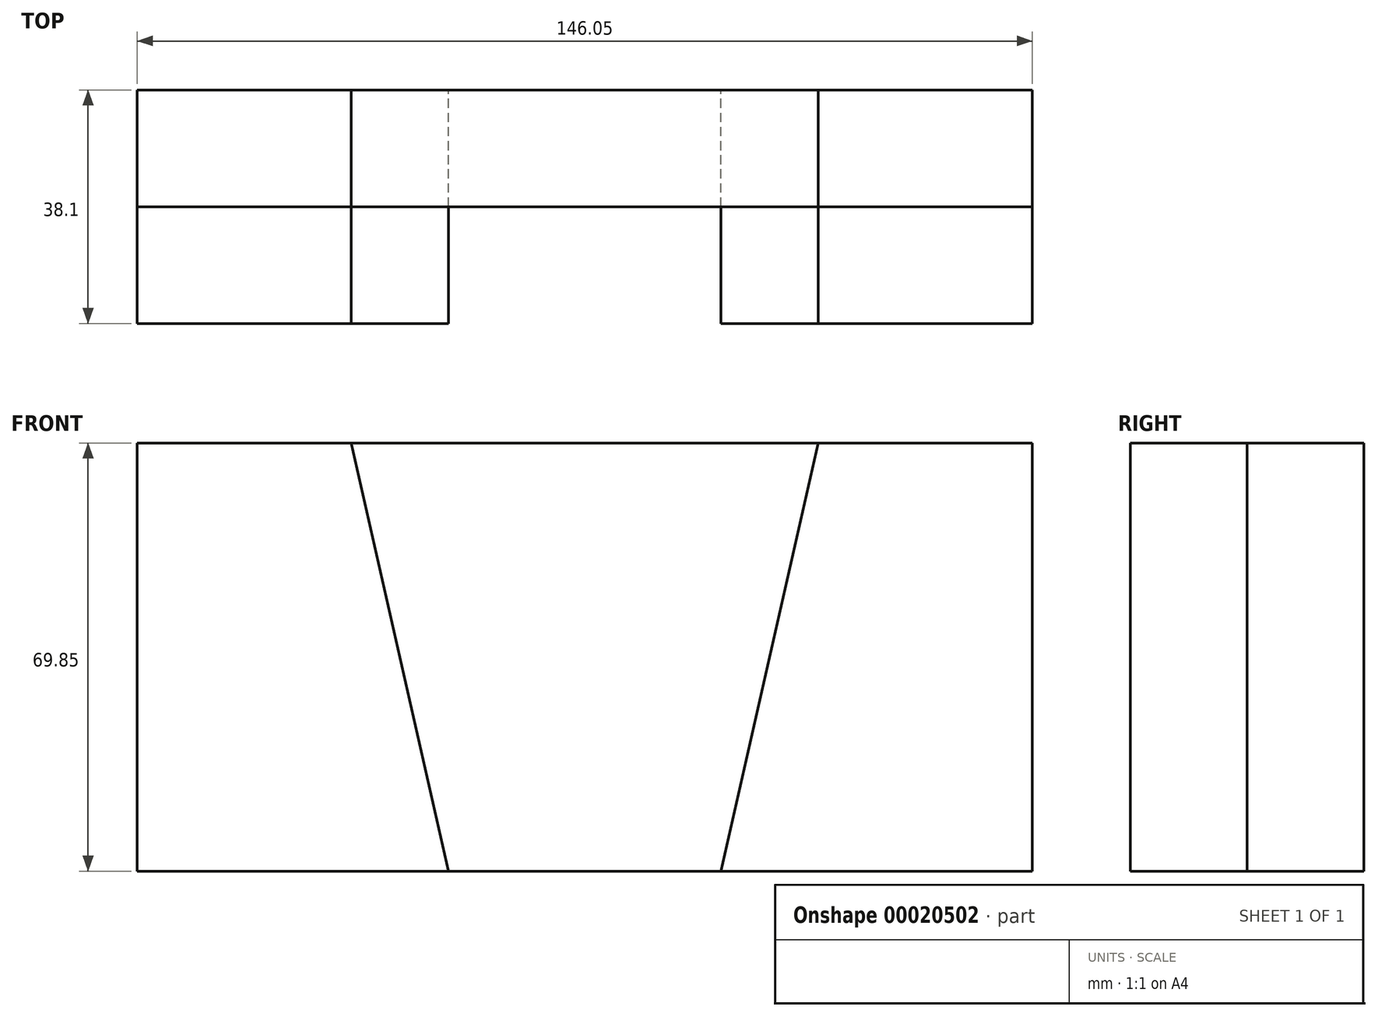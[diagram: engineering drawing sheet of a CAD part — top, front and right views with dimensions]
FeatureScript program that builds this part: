
annotation { "Feature Type Name" : "Feature", "Feature Type Description" : "" }
export const myFeature = defineFeature(function(context is Context, id is Id, definition is map)
    precondition{}
    {
        {
            var Q0;
            Q0=qCreatedBy(makeId("Front.planeOp"),FACE);
            var sketch = newSketch(context, id + "F0", { "sketchPlane" : qUnion([Q0])});
            skPoint(sketch, "E0.start.orphan", {"position": v(-6.14, 26.79) * mm});
            skPoint(sketch, "E1.start.orphan", {"position": v(33.32, 40.14) * mm});
            skPoint(sketch, "E2.orphan", {"position": v(-45.6, 13.44) * mm});
            skLineSegment(sketch, "E3", {"start": v(-65.63, 71.67) * mm, "end": v(-65.63, 1.82) * mm});
            skLineSegment(sketch, "E4", {"start": v(-65.63, 71.67) * mm, "end": v(-30.7, 71.67) * mm});
            skLineSegment(sketch, "E5", {"start": v(-65.63, 1.82) * mm, "end": v(-14.83, 1.82) * mm});
            skLineSegment(sketch, "E6", {"start": v(-30.7, 71.67) * mm, "end": v(-14.83, 1.82) * mm});
            skLineSegment(sketch, "E7", {"start": v(-30.7, 71.67) * mm, "end": v(45.5, 71.67) * mm});
            skLineSegment(sketch, "E8", {"start": v(45.5, 71.67) * mm, "end": v(80.42, 71.67) * mm});
            skLineSegment(sketch, "E9", {"start": v(80.42, 71.67) * mm, "end": v(80.42, 1.82) * mm});
            skLineSegment(sketch, "E10", {"start": v(-14.83, 1.82) * mm, "end": v(29.62, 1.82) * mm});
            skLineSegment(sketch, "E11", {"start": v(29.62, 1.82) * mm, "end": v(80.42, 1.82) * mm});
            skLineSegment(sketch, "E12", {"start": v(29.62, 1.82) * mm, "end": v(45.5, 71.67) * mm});
            skSolve(sketch);
        }
        {
            var Q0;
            Q0=makeQuery(id+"F0.imprint","IMPRINT",FACE,{"disambiguationData":[TD([[makeQuery(id+"F0.imprint","IMPRINT",EDGE,{"derivedFrom":sQuery(id+"F0.wireOp",EDGE,"E3")}),1.0]])]});
            var Q1;
            Q1=makeQuery(id+"F0.imprint","IMPRINT",FACE,{"disambiguationData":[TD([[makeQuery(id+"F0.imprint","IMPRINT",EDGE,{"derivedFrom":sQuery(id+"F0.wireOp",EDGE,"E8")}),-1.0]])]});
            extrude(context, id + "F1", {"entities" : qUnion([Q0, Q1]), "depth" : 38.1 * mm});
        }
        {
            var Q0;
            Q0 = qSketchRegion(id + "F0", true);
            extrude(context, id + "F2", {"entities" : qUnion([Q0]), "depth" : 19.05 * mm});
        }
    });
